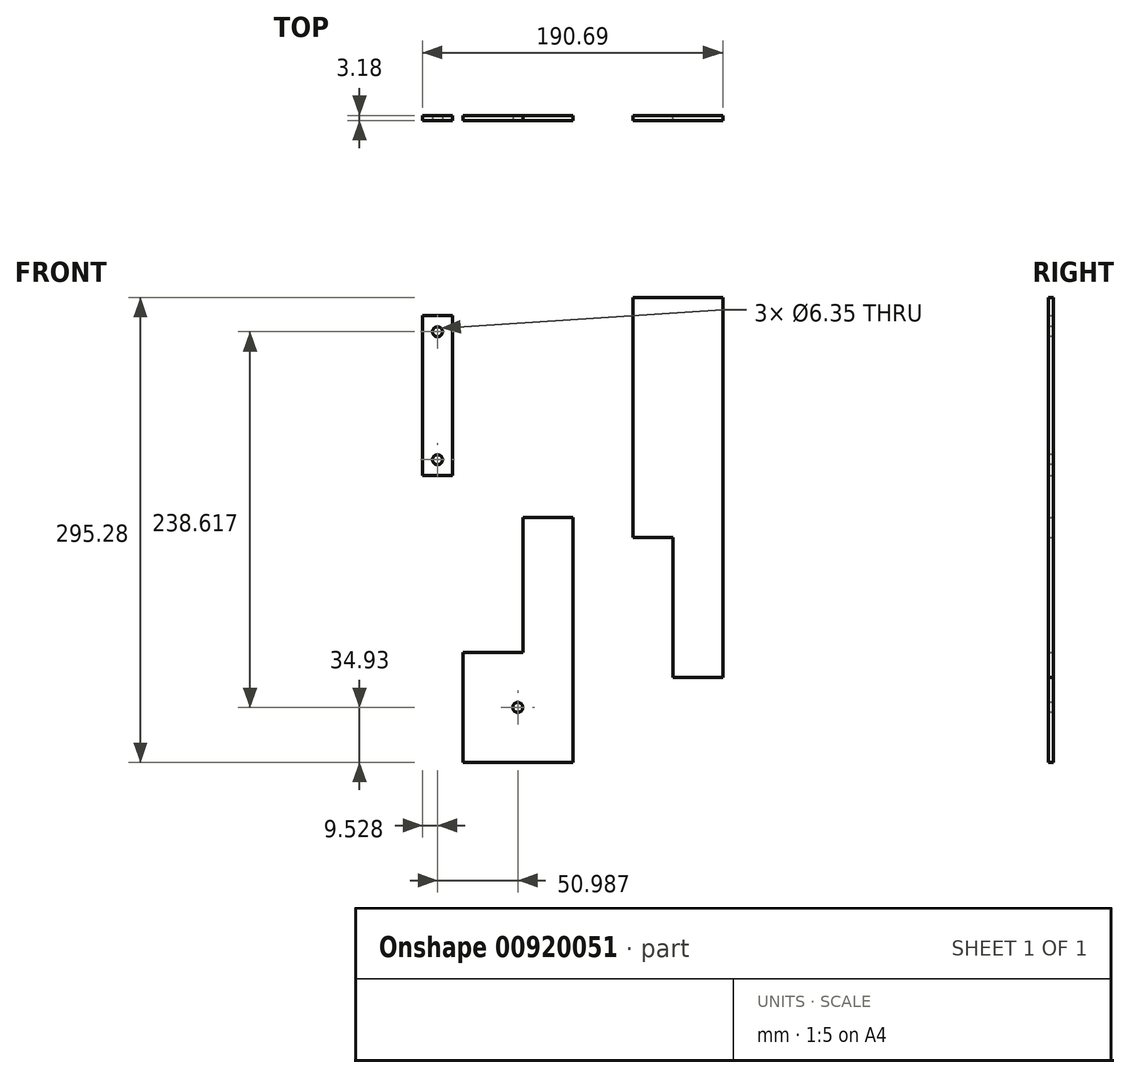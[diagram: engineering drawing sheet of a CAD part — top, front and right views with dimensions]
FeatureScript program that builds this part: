
annotation { "Feature Type Name" : "Feature", "Feature Type Description" : "" }
export const myFeature = defineFeature(function(context is Context, id is Id, definition is map)
    precondition{}
    {
        {
            var Q0;
            Q0=qCreatedBy(makeId("Front.planeOp"),FACE);
            var sketch = newSketch(context, id + "F0", { "sketchPlane" : qUnion([Q0])});
            skLineSegment(sketch, "E0.bottom", {"start": v(0, 152.4) * mm, "end": v(57.15, 152.4) * mm});
            skLineSegment(sketch, "E0.top", {"start": v(0, 0) * mm, "end": v(25.4, 0) * mm});
            skLineSegment(sketch, "E0.left", {"start": v(0, 152.4) * mm, "end": v(0, 0) * mm});
            skLineSegment(sketch, "E0.right", {"start": v(57.15, 152.4) * mm, "end": v(57.15, 0) * mm});
            skLineSegment(sketch, "E1.top", {"start": v(57.15, -88.9) * mm, "end": v(25.4, -88.9) * mm});
            skLineSegment(sketch, "E1.left", {"start": v(57.15, 0) * mm, "end": v(57.15, -88.9) * mm});
            skLineSegment(sketch, "E1.right", {"start": v(25.4, 0) * mm, "end": v(25.4, -88.9) * mm});
            skSolve(sketch);
        }
        {
            var Q0;
            Q0=makeQuery(id+"F0.imprint","IMPRINT",FACE,{"disambiguationData":[TD([[makeQuery(id+"F0.imprint","IMPRINT",EDGE,{"derivedFrom":sQuery(id+"F0.wireOp",EDGE,"E0.bottom")}),-1.0]])]});
            extrude(context, id + "F1", {"entities" : qUnion([Q0]), "depth" : 3.17 * mm, "offsetDistance" : 25.4 * mm});
        }
        {
            var Q0;
            Q0=qCreatedBy(makeId("Front.planeOp"),FACE);
            var sketch = newSketch(context, id + "F2", { "sketchPlane" : qUnion([Q0])});
            skLineSegment(sketch, "E2.bottom", {"start": v(-69.85, 0) * mm, "end": v(-38.1, 0) * mm});
            skLineSegment(sketch, "E2.top", {"start": v(-69.85, -111.13) * mm, "end": v(-38.1, -111.13) * mm});
            skLineSegment(sketch, "E2.left", {"start": v(-69.85, 0) * mm, "end": v(-69.85, -73.02) * mm});
            skLineSegment(sketch, "E2.right", {"start": v(-38.1, 0) * mm, "end": v(-38.1, -111.13) * mm});
            skLineSegment(sketch, "E3.bottom", {"start": v(-69.85, -73.02) * mm, "end": v(-107.95, -73.02) * mm});
            skLineSegment(sketch, "E3.top", {"start": v(-38.1, -111.13) * mm, "end": v(-107.95, -111.13) * mm});
            skLineSegment(sketch, "E3.left", {"start": v(-38.1, -73.02) * mm, "end": v(-38.1, -111.13) * mm});
            skLineSegment(sketch, "E3.right", {"start": v(-107.95, -73.02) * mm, "end": v(-107.95, -111.13) * mm});
            skSolve(sketch);
        }
        {
            var Q0;
            Q0=makeQuery(id+"F2.imprint","IMPRINT",FACE,{"disambiguationData":[TD([[makeQuery(id+"F2.imprint","IMPRINT",EDGE,{"derivedFrom":sQuery(id+"F2.wireOp",EDGE,"E2.bottom")}),-1.0]])]});
            extrude(context, id + "F3", {"entities" : qUnion([Q0]), "depth" : 3.17 * mm, "offsetDistance" : 25.4 * mm});
        }
        {
            var Q0;
            Q0=makeQuery(id+"F3.opExtrude","SWEPT_FACE",FACE,{"disambiguationData":[OSD([sQuery(id+"F2.wireOp",EDGE,"E3.top")])]});
            extrude(context, id + "F4", {"entities" : qUnion([Q0]), "operationType" : NewBodyOperationType.ADD, "depth" : 31.75 * mm, "offsetDistance" : 25.4 * mm});
        }
        {
            var Q0;
            Q0=makeQuery(id+"F3.opExtrude","SWEPT_FACE",FACE,{"disambiguationData":[OSD([sQuery(id+"F2.wireOp",EDGE,"E2.bottom")])]});
            extrude(context, id + "F5", {"entities" : qUnion([Q0]), "operationType" : NewBodyOperationType.ADD, "depth" : 12.7 * mm, "offsetDistance" : 25.4 * mm});
        }
        {
            var Q0;
            {var subQ0=sQuery(id+"F2.wireOp",EDGE,"E2.bottom");var subQ1=sQuery(id+"F2.wireOp",EDGE,"E3.top");Q0=makeQuery(id+"F5.boolean.opBoolean","MERGE",FACE,{"derivedFrom":[makeQuery(id+"F4.boolean.opBoolean","MERGE",FACE,{"derivedFrom":[makeQuery(id+"F3.opExtrude","CAP_FACE",FACE,{"disambiguationData":[OSD([subQ0,sQuery(id+"F2.wireOp",EDGE,"E2.left"),sQuery(id+"F2.wireOp",EDGE,"E2.right"),sQuery(id+"F2.wireOp",EDGE,"E3.bottom"),subQ1,sQuery(id+"F2.wireOp",EDGE,"E3.left"),sQuery(id+"F2.wireOp",EDGE,"E3.right")])],"isStart":false}),makeQuery(id+"F4.opExtrude","SWEPT_FACE",FACE,{"disambiguationData":[OSD([subQ1]),TDD([makeQuery(id+"F3.opExtrude","CAP_EDGE",EDGE,{"disambiguationData":[OSD([subQ1])],"isStart":false})])]})]}),makeQuery(id+"F5.opExtrude","SWEPT_FACE",FACE,{"disambiguationData":[OSD([subQ0]),TDD([makeQuery(id+"F3.opExtrude","CAP_EDGE",EDGE,{"disambiguationData":[OSD([subQ0])],"isStart":false})])]})]});}
            var sketch = newSketch(context, id + "F6", { "sketchPlane" : qUnion([Q0])});
            skCircle(sketch, "E4", {"center": v(-73.02, -107.95) * mm, "radius": 3.18 * mm});
            skPoint(sketch, "E4.centerSnap0", {"position": v(-107.95, -107.95) * mm});
            skLineSegment(sketch, "E5", {"start": v(-107.95, -107.95) * mm, "end": v(-73.02, -107.95) * mm, "construction": true});
            skLineSegment(sketch, "E6", {"start": v(-73.02, -142.88) * mm, "end": v(-73.02, -107.95) * mm, "construction": true});
            skSolve(sketch);
        }
        {
            var Q0;
            Q0=makeQuery(id+"F6.imprint","IMPRINT",FACE,{"disambiguationData":[TD([[makeQuery(id+"F6.imprint","IMPRINT",EDGE,{"derivedFrom":sQuery(id+"F6.wireOp",EDGE,"E4")}),1.0]])]});
            extrude(context, id + "F7", {"entities" : qUnion([Q0]), "operationType" : NewBodyOperationType.REMOVE, "oppositeDirection" : true, "depth" : 25.4 * mm, "offsetDistance" : 25.4 * mm});
        }
        {
            var Q0;
            Q0=qCreatedBy(makeId("Front.planeOp"),FACE);
            var sketch = newSketch(context, id + "F8", { "sketchPlane" : qUnion([Q0])});
            skLineSegment(sketch, "E7.bottom", {"start": v(-133.54, 140.83) * mm, "end": v(-114.49, 140.83) * mm});
            skLineSegment(sketch, "E7.top", {"start": v(-133.54, 39.23) * mm, "end": v(-114.49, 39.23) * mm});
            skLineSegment(sketch, "E7.left", {"start": v(-133.54, 140.83) * mm, "end": v(-133.54, 39.23) * mm});
            skLineSegment(sketch, "E7.right", {"start": v(-114.49, 140.83) * mm, "end": v(-114.49, 39.23) * mm});
            skSolve(sketch);
        }
        {
            var Q0;
            Q0=makeQuery(id+"F8.imprint","IMPRINT",FACE,{"disambiguationData":[TD([[makeQuery(id+"F8.imprint","IMPRINT",EDGE,{"derivedFrom":sQuery(id+"F8.wireOp",EDGE,"E7.bottom")}),-1.0]])]});
            extrude(context, id + "F9", {"entities" : qUnion([Q0]), "depth" : 3.17 * mm, "offsetDistance" : 25.4 * mm});
        }
        {
            var Q0;
            Q0=makeQuery(id+"F9.opExtrude","CAP_FACE",FACE,{"disambiguationData":[OSD([sQuery(id+"F8.wireOp",EDGE,"E7.bottom"),sQuery(id+"F8.wireOp",EDGE,"E7.top"),sQuery(id+"F8.wireOp",EDGE,"E7.left"),sQuery(id+"F8.wireOp",EDGE,"E7.right")])],"isStart":false});
            var sketch = newSketch(context, id + "F10", { "sketchPlane" : qUnion([Q0])});
            skCircle(sketch, "E8", {"center": v(-124.01, 130.67) * mm, "radius": 3.18 * mm});
            skCircle(sketch, "E9", {"center": v(-124.01, 49.39) * mm, "radius": 3.18 * mm});
            skLineSegment(sketch, "E10", {"start": v(-124.01, 140.83) * mm, "end": v(-124.01, 39.23) * mm, "construction": true});
            skLineSegment(sketch, "E11", {"start": v(-133.54, 130.67) * mm, "end": v(-114.49, 130.67) * mm, "construction": true});
            skLineSegment(sketch, "E12", {"start": v(-133.54, 49.39) * mm, "end": v(-114.49, 49.39) * mm, "construction": true});
            skSolve(sketch);
        }
        {
            var Q0;
            Q0=makeQuery(id+"F10.imprint","IMPRINT",FACE,{"disambiguationData":[TD([[makeQuery(id+"F10.imprint","IMPRINT",EDGE,{"derivedFrom":sQuery(id+"F10.wireOp",EDGE,"E8")}),1.0]])]});
            var Q1;
            Q1=makeQuery(id+"F10.imprint","IMPRINT",FACE,{"disambiguationData":[TD([[makeQuery(id+"F10.imprint","IMPRINT",EDGE,{"derivedFrom":sQuery(id+"F10.wireOp",EDGE,"E9")}),1.0]])]});
            extrude(context, id + "F11", {"entities" : qUnion([Q0, Q1]), "operationType" : NewBodyOperationType.REMOVE, "oppositeDirection" : true, "depth" : 25.4 * mm, "offsetDistance" : 25.4 * mm});
        }
    });
